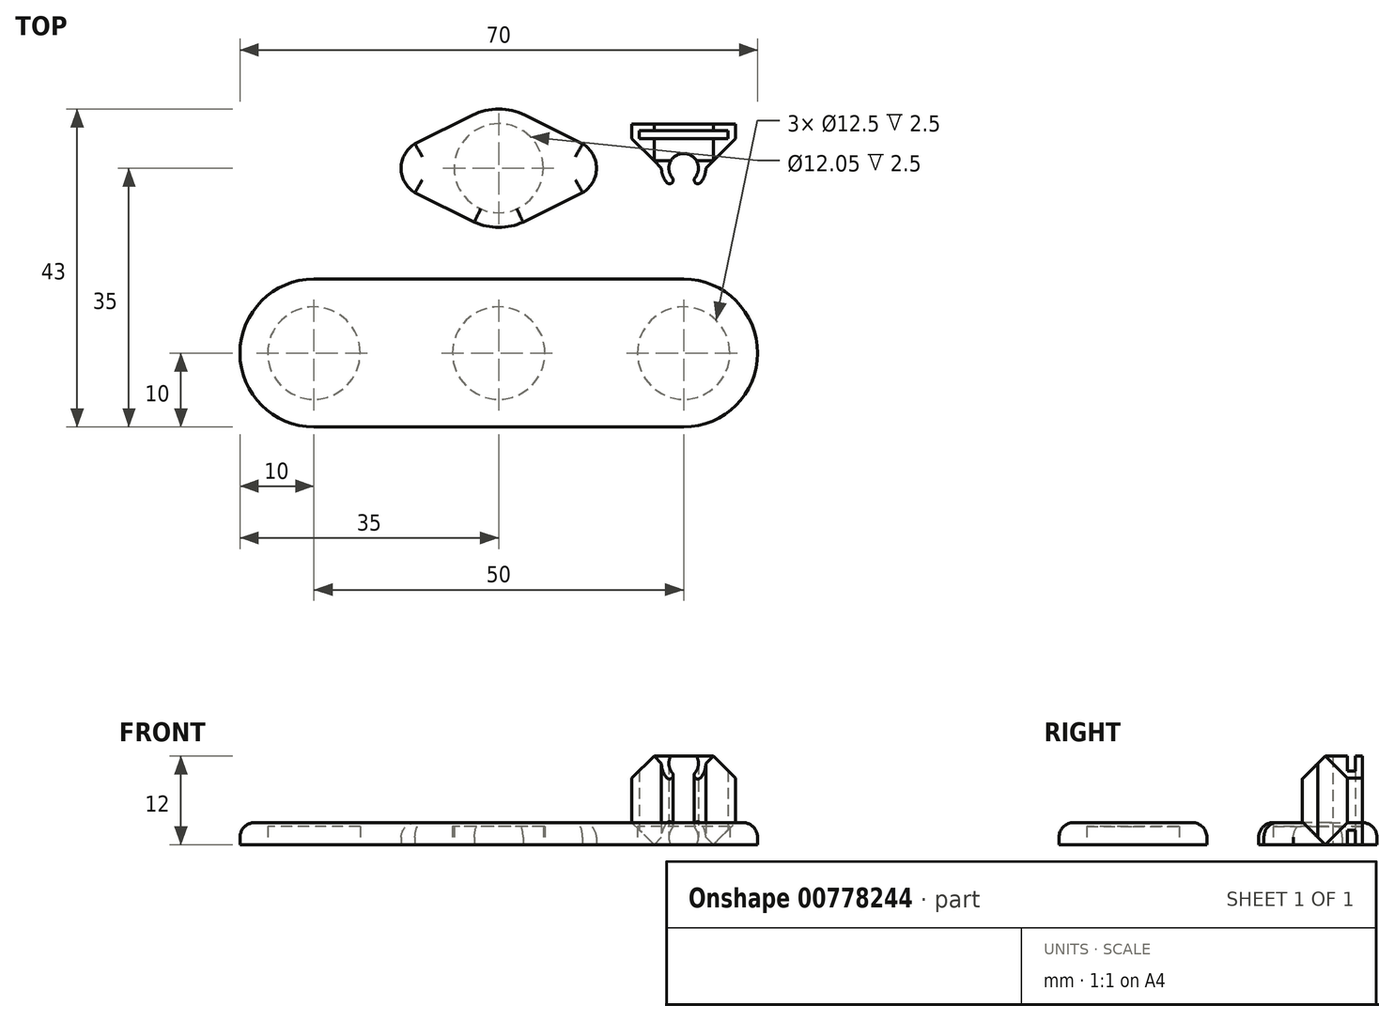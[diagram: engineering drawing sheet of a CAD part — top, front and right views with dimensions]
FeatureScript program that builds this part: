
annotation { "Feature Type Name" : "Feature", "Feature Type Description" : "" }
export const myFeature = defineFeature(function(context is Context, id is Id, definition is map)
    precondition{}
    {
        {
            var Q0;
            Q0=qCreatedBy(makeId("Top.planeOp"),FACE);
            var sketch = newSketch(context, id + "F0", { "sketchPlane" : qUnion([Q0])});
            skLineSegment(sketch, "E0", {"start": v(-25, -15) * mm, "end": v(25, -15) * mm});
            skLineSegment(sketch, "E1", {"start": v(25, -15) * mm, "end": v(25, -35) * mm, "construction": true});
            skLineSegment(sketch, "E2", {"start": v(25, -35) * mm, "end": v(-25, -35) * mm});
            skLineSegment(sketch, "E3", {"start": v(-25, -35) * mm, "end": v(-25, -15) * mm, "construction": true});
            skCircle(sketch, "E4", {"center": v(0, 0) * mm, "radius": 6.03 * mm});
            skArc(sketch, "E5", {"start": v(-25, -15) * mm, "mid": v(-35, -25) * mm, "end": v(-25, -35) * mm});
            skArc(sketch, "E6", {"start": v(25, -35) * mm, "mid": v(35, -25) * mm, "end": v(25, -15) * mm});
            skCircle(sketch, "E7", {"center": v(0, 0) * mm, "radius": 8 * mm});
            skPoint(sketch, "E8", {"position": v(0, -15) * mm});
            skCircle(sketch, "E9", {"center": v(-25, -25) * mm, "radius": 6.25 * mm});
            skCircle(sketch, "E10", {"center": v(25, -25) * mm, "radius": 6.25 * mm});
            skCircle(sketch, "E11", {"center": v(0, -25) * mm, "radius": 6.25 * mm});
            skLineSegment(sketch, "E12", {"start": v(-18, 0) * mm, "end": v(-3.56, 7.17) * mm});
            skLineSegment(sketch, "E13", {"start": v(-18, 0) * mm, "end": v(-3.3, -7.3) * mm});
            skArc(sketch, "E14", {"start": v(-10.78, 3.58) * mm, "mid": v(-13.2, 0) * mm, "end": v(-10.78, -3.58) * mm});
            skPoint(sketch, "E14.endSnap0", {"position": v(-10.78, 3.58) * mm});
            skLineSegment(sketch, "E15", {"start": v(0, 0) * mm, "end": v(0, 13.2) * mm, "construction": true});
            skLineSegment(sketch, "E16.MirrorCS", {"start": v(18, 0) * mm, "end": v(3.3, -7.3) * mm});
            skArc(sketch, "E17.MirrorCS", {"start": v(10.78, 3.58) * mm, "mid": v(13.2, 0) * mm, "end": v(10.78, -3.58) * mm});
            skLineSegment(sketch, "E18.MirrorCS", {"start": v(18, 0) * mm, "end": v(3.56, 7.17) * mm});
            skCircle(sketch, "E19", {"center": v(25, 0) * mm, "radius": 2 * mm});
            skCircle(sketch, "E20", {"center": v(25, 0) * mm, "radius": 3 * mm});
            skLineSegment(sketch, "E21", {"start": v(25, 0) * mm, "end": v(25, -4.45) * mm, "construction": true});
            skLineSegment(sketch, "E22", {"start": v(25, 0) * mm, "end": v(28.52, -2.96) * mm, "construction": true});
            skArc(sketch, "E23", {"start": v(26.53, -1.29) * mm, "mid": v(26.6, -1.99) * mm, "end": v(27.3, -1.93) * mm});
            skArc(sketch, "E24.MirrorCS", {"start": v(23.47, -1.29) * mm, "mid": v(23.4, -1.99) * mm, "end": v(22.7, -1.93) * mm});
            skLineSegment(sketch, "E25", {"start": v(22, 0) * mm, "end": v(18, 4) * mm});
            skLineSegment(sketch, "E26", {"start": v(18, 4) * mm, "end": v(32, 4) * mm});
            skLineSegment(sketch, "E27", {"start": v(32, 4) * mm, "end": v(28, 0) * mm});
            skLineSegment(sketch, "E28", {"start": v(22, 0) * mm, "end": v(22, 6.24) * mm, "construction": true});
            skLineSegment(sketch, "E29", {"start": v(28, 0) * mm, "end": v(28, 6.43) * mm, "construction": true});
            skLineSegment(sketch, "E30.bottom", {"start": v(18, 4) * mm, "end": v(18, 4) * mm});
            skLineSegment(sketch, "E31", {"start": v(18, 4) * mm, "end": v(18, 6) * mm});
            skLineSegment(sketch, "E32", {"start": v(18, 6) * mm, "end": v(32, 6) * mm});
            skLineSegment(sketch, "E33", {"start": v(32, 6) * mm, "end": v(32, 4) * mm});
            skLineSegment(sketch, "E34", {"start": v(19, 4) * mm, "end": v(19, 5.1) * mm});
            skLineSegment(sketch, "E35", {"start": v(19, 5.1) * mm, "end": v(31, 5.1) * mm});
            skLineSegment(sketch, "E36", {"start": v(31, 5.1) * mm, "end": v(31, 4) * mm});
            skSolve(sketch);
        }
        {
            var Q0;
            Q0=makeQuery(id+"F0.imprint","IMPRINT",FACE,{"disambiguationData":[TD([[makeQuery(id+"F0.imprint","IMPRINT",EDGE,{"derivedFrom":sQuery(id+"F0.wireOp",EDGE,"E0")}),-1.0]])]});
            var Q1;
            Q1=makeQuery(id+"F0.imprint","IMPRINT",FACE,{"disambiguationData":[TD([[makeQuery(id+"F0.imprint","IMPRINT",EDGE,{"derivedFrom":sQuery(id+"F0.wireOp",EDGE,"E4")}),-1.0]])]});
            var Q2;
            Q2=makeQuery(id+"F0.imprint","IMPRINT",FACE,{"disambiguationData":[TD([[makeQuery(id+"F0.imprint","IMPRINT",EDGE,{"derivedFrom":sQuery(id+"F0.wireOp",EDGE,"E4")}),1.0]])]});
            var Q3;
            Q3=makeQuery(id+"F0.imprint","IMPRINT",FACE,{"disambiguationData":[TD([[makeQuery(id+"F0.imprint","IMPRINT",EDGE,{"derivedFrom":sQuery(id+"F0.wireOp",EDGE,"E9")}),1.0]])]});
            var Q4;
            Q4=makeQuery(id+"F0.imprint","IMPRINT",FACE,{"disambiguationData":[TD([[makeQuery(id+"F0.imprint","IMPRINT",EDGE,{"derivedFrom":sQuery(id+"F0.wireOp",EDGE,"E11")}),1.0]])]});
            var Q5;
            Q5=makeQuery(id+"F0.imprint","IMPRINT",FACE,{"disambiguationData":[TD([[makeQuery(id+"F0.imprint","IMPRINT",EDGE,{"derivedFrom":sQuery(id+"F0.wireOp",EDGE,"E10")}),1.0]])]});
            var Q6;
            {var subQ0=sQuery(id+"F0.wireOp",EDGE,"E12");var subQ1=sQuery(id+"F0.wireOp",EDGE,"E7");var subQ2=makeQuery(id+"F0.imprint","INTERSECT",VERTEX,{"derivedFrom":[subQ1,subQ0]});Q6=makeQuery(id+"F0.imprint","IMPRINT",FACE,{"disambiguationData":[TD([[makeQuery(id+"F0.imprint","IMPRINT",EDGE,{"disambiguationData":[TD([[subQ2,-1.0]])],"derivedFrom":subQ1}),-1.0]])]});}
            var Q7;
            {var subQ1=sQuery(id+"F0.wireOp",EDGE,"E16.MirrorCS");var subQ6=sQuery(id+"F0.wireOp",EDGE,"E7");var subQ7=makeQuery(id+"F0.imprint","INTERSECT",VERTEX,{"derivedFrom":[subQ6,subQ1]});Q7=makeQuery(id+"F0.imprint","IMPRINT",FACE,{"disambiguationData":[TD([[makeQuery(id+"F0.imprint","IMPRINT",EDGE,{"disambiguationData":[TD([[subQ7,-1.0]])],"derivedFrom":subQ6}),-1.0]])]});}
            extrude(context, id + "F1", {"entities" : qUnion([Q0, Q1, Q2, Q3, Q4, Q5, Q6, Q7]), "depth" : 3 * mm, "offsetDistance" : 25 * mm});
        }
        {
            var Q0;
            Q0=makeQuery(id+"F0.imprint","IMPRINT",FACE,{"disambiguationData":[TD([[makeQuery(id+"F0.imprint","IMPRINT",EDGE,{"derivedFrom":sQuery(id+"F0.wireOp",EDGE,"E4")}),1.0]])]});
            var Q1;
            Q1=makeQuery(id+"F0.imprint","IMPRINT",FACE,{"disambiguationData":[TD([[makeQuery(id+"F0.imprint","IMPRINT",EDGE,{"derivedFrom":sQuery(id+"F0.wireOp",EDGE,"E9")}),1.0]])]});
            var Q2;
            Q2=makeQuery(id+"F0.imprint","IMPRINT",FACE,{"disambiguationData":[TD([[makeQuery(id+"F0.imprint","IMPRINT",EDGE,{"derivedFrom":sQuery(id+"F0.wireOp",EDGE,"E11")}),1.0]])]});
            var Q3;
            Q3=makeQuery(id+"F0.imprint","IMPRINT",FACE,{"disambiguationData":[TD([[makeQuery(id+"F0.imprint","IMPRINT",EDGE,{"derivedFrom":sQuery(id+"F0.wireOp",EDGE,"E10")}),1.0]])]});
            extrude(context, id + "F2", {"entities" : qUnion([Q0, Q1, Q2, Q3]), "operationType" : NewBodyOperationType.REMOVE, "depth" : 2.5 * mm, "offsetDistance" : 25 * mm});
        }
        {
            var Q0;
            Q0=makeQuery(id+"F1.opExtrude","CAP_EDGE",EDGE,{"disambiguationData":[OSD([sQuery(id+"F0.wireOp",EDGE,"E16.MirrorCS")])],"isStart":false});
            var Q1;
            {var subQ0=sQuery(id+"F0.wireOp",EDGE,"E7");Q1=makeQuery(id+"F1.opExtrude","CAP_EDGE",EDGE,{"disambiguationData":[OSD([subQ0]),TDD([makeQuery(id+"F0.imprint","IMPRINT",EDGE,{"disambiguationData":[TD([[makeQuery(id+"F0.imprint","INTERSECT",VERTEX,{"derivedFrom":[subQ0,sQuery(id+"F0.wireOp",EDGE,"E13")]}),-1.0]])],"derivedFrom":subQ0})])],"isStart":false});}
            var Q2;
            Q2=makeQuery(id+"F1.opExtrude","CAP_EDGE",EDGE,{"disambiguationData":[OSD([sQuery(id+"F0.wireOp",EDGE,"E13")])],"isStart":false});
            var Q3;
            Q3=makeQuery(id+"F1.opExtrude","CAP_EDGE",EDGE,{"disambiguationData":[OSD([sQuery(id+"F0.wireOp",EDGE,"E17.MirrorCS")])],"isStart":false});
            var Q4;
            Q4=makeQuery(id+"F1.opExtrude","CAP_EDGE",EDGE,{"disambiguationData":[OSD([sQuery(id+"F0.wireOp",EDGE,"E18.MirrorCS")])],"isStart":false});
            var Q5;
            Q5=makeQuery(id+"F1.opExtrude","CAP_EDGE",EDGE,{"disambiguationData":[OSD([sQuery(id+"F0.wireOp",EDGE,"E14")])],"isStart":false});
            var Q6;
            Q6=makeQuery(id+"F1.opExtrude","CAP_EDGE",EDGE,{"disambiguationData":[OSD([sQuery(id+"F0.wireOp",EDGE,"E5")])],"isStart":false});
            fillet(context, id + "F3", {"entities" : qUnion([Q0, Q1, Q2, Q3, Q4, Q5, Q6]), "radius" : 2 * mm, "tangentPropagation" : true, "allowEdgeOverflow" : false});
        }
        {
            var Q0;
            {var subQ0=sQuery(id+"F0.wireOp",EDGE,"E25");Q0=makeQuery(id+"F0.imprint","IMPRINT",FACE,{"disambiguationData":[TD([[makeQuery(id+"F0.imprint","IMPRINT",EDGE,{"derivedFrom":subQ0}),-1.0]])]});}
            var Q1;
            {var subQ3=sQuery(id+"F0.wireOp",EDGE,"E31");Q1=makeQuery(id+"F0.imprint","IMPRINT",FACE,{"disambiguationData":[TD([[makeQuery(id+"F0.imprint","IMPRINT",EDGE,{"derivedFrom":subQ3}),-1.0]])]});}
            var Q2;
            {var subQ0=sQuery(id+"F0.wireOp",EDGE,"E27");Q2=makeQuery(id+"F0.imprint","IMPRINT",FACE,{"disambiguationData":[TD([[makeQuery(id+"F0.imprint","IMPRINT",EDGE,{"derivedFrom":subQ0}),-1.0]])]});}
            var Q3;
            {var subQ5=sQuery(id+"F0.wireOp",EDGE,"E23");Q3=makeQuery(id+"F0.imprint","IMPRINT",FACE,{"disambiguationData":[TD([[makeQuery(id+"F0.imprint","IMPRINT",EDGE,{"derivedFrom":subQ5}),1.0]])]});}
            extrude(context, id + "F4", {"entities" : qUnion([Q0, Q1, Q2, Q3]), "depth" : 12 * mm, "offsetDistance" : 25 * mm});
        }
        {
            var Q0;
            Q0=makeQuery(id+"F4.opExtrude","CAP_EDGE",EDGE,{"disambiguationData":[OSD([sQuery(id+"F0.wireOp",EDGE,"E33")])],"isStart":false});
            var Q1;
            Q1=makeQuery(id+"F4.opExtrude","CAP_EDGE",EDGE,{"disambiguationData":[OSD([sQuery(id+"F0.wireOp",EDGE,"E31")])],"isStart":false});
            var Q2;
            Q2=makeQuery(id+"F4.opExtrude","CAP_EDGE",EDGE,{"disambiguationData":[OSD([sQuery(id+"F0.wireOp",EDGE,"E33")])],"isStart":true});
            var Q3;
            Q3=makeQuery(id+"F4.opExtrude","CAP_EDGE",EDGE,{"disambiguationData":[OSD([sQuery(id+"F0.wireOp",EDGE,"E31")])],"isStart":true});
            chamfer(context, id + "F5", {"entities" : qUnion([Q0, Q1, Q2, Q3]), "width" : 3 * mm, "tangentPropagation" : true});
        }
        {
            var Q0;
            Q0=qCreatedBy(makeId("Right.planeOp"),FACE);
            cPlane(context, id + "F6", {"entities" : qUnion([Q0]), "cplaneType" : CPlaneType.OFFSET, "offset" : 25 * mm, "width" : 150 * mm, "height" : 150 * mm});
        }
        {
            var Q0;
            Q0=qCreatedBy(id+"F6.planeOp",FACE);
            var sketch = newSketch(context, id + "F7", { "sketchPlane" : qUnion([Q0])});
            skLineSegment(sketch, "E37", {"start": v(-3.35, 0) * mm, "end": v(-3.35, 4.35) * mm});
            skLineSegment(sketch, "E38", {"start": v(-3.35, 4.35) * mm, "end": v(1, 0) * mm});
            skLineSegment(sketch, "E39", {"start": v(-3.35, 0) * mm, "end": v(1, 0) * mm});
            skPoint(sketch, "E40", {"position": v(4, 0) * mm});
            skLineSegment(sketch, "E41", {"start": v(0, 6) * mm, "end": v(-5.43, 6) * mm, "construction": true});
            skLineSegment(sketch, "E42.MirrorCS", {"start": v(-3.35, 7.65) * mm, "end": v(1, 12) * mm});
            skLineSegment(sketch, "E43.MirrorCS", {"start": v(-3.35, 12) * mm, "end": v(-3.35, 7.65) * mm});
            skLineSegment(sketch, "E44.MirrorCS", {"start": v(-3.35, 12) * mm, "end": v(1, 12) * mm});
            skSolve(sketch);
        }
        {
            var Q0;
            Q0=makeQuery(id+"F7.imprint","IMPRINT",FACE,{"disambiguationData":[TD([[makeQuery(id+"F7.imprint","IMPRINT",EDGE,{"derivedFrom":sQuery(id+"F7.wireOp",EDGE,"E37")}),-1.0]])]});
            var Q1;
            Q1=makeQuery(id+"F7.imprint","IMPRINT",FACE,{"disambiguationData":[TD([[makeQuery(id+"F7.imprint","IMPRINT",EDGE,{"derivedFrom":sQuery(id+"F7.wireOp",EDGE,"E42.MirrorCS")}),1.0]])]});
            extrude(context, id + "F8", {"entities" : qUnion([Q0, Q1]), "operationType" : NewBodyOperationType.REMOVE, "endBound" : BoundingType.SYMMETRIC, "oppositeDirection" : true, "depth" : 10 * mm, "offsetDistance" : 25 * mm});
        }
    });
